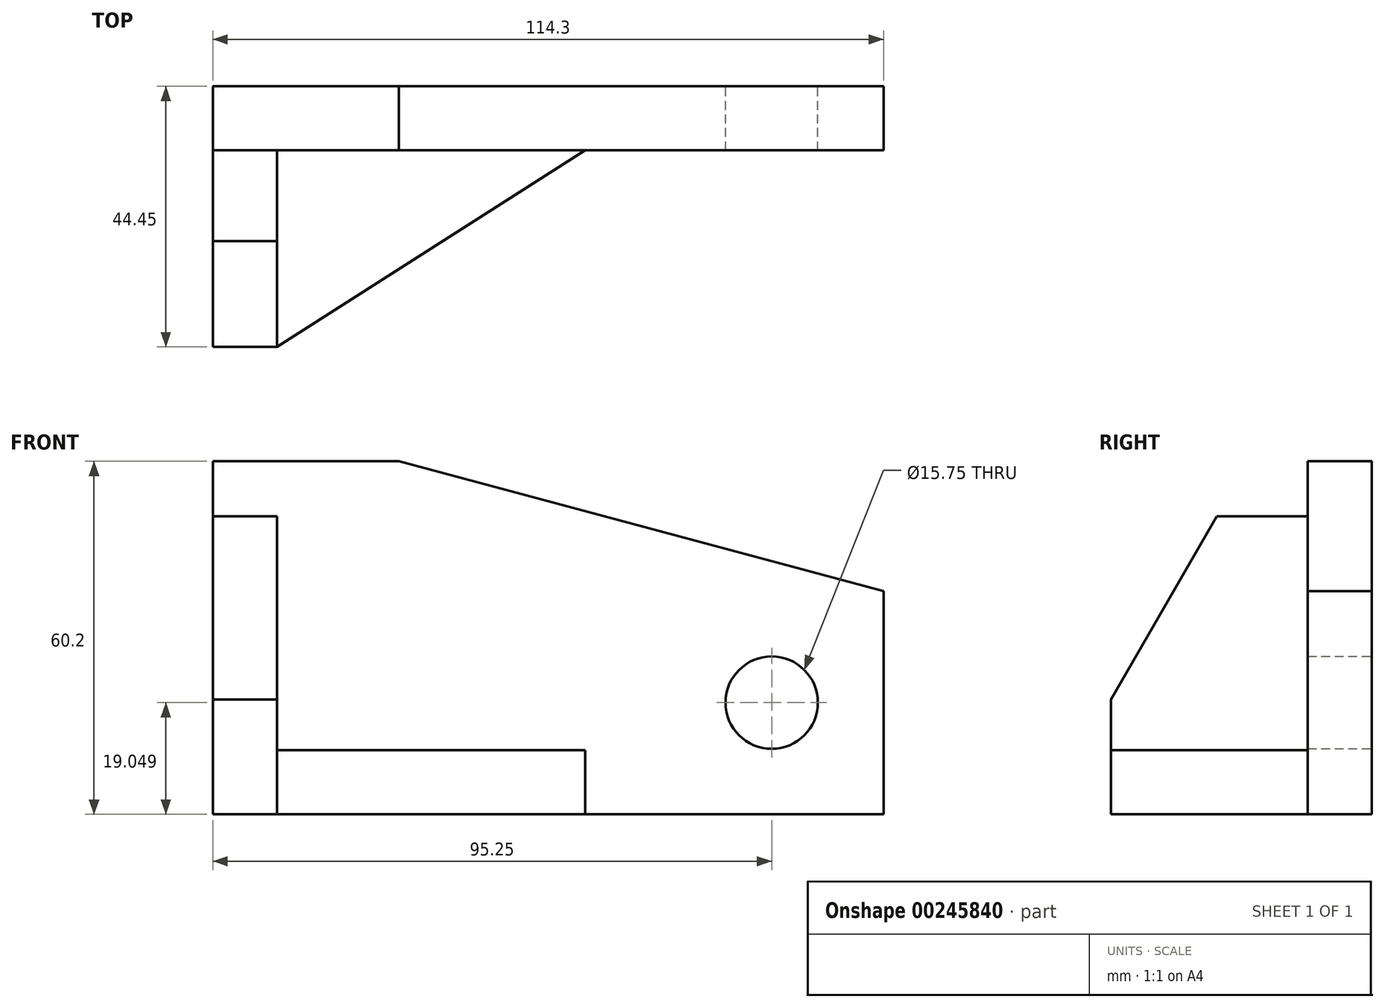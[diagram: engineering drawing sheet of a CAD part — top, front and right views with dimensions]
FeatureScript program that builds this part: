
annotation { "Feature Type Name" : "Feature", "Feature Type Description" : "" }
export const myFeature = defineFeature(function(context is Context, id is Id, definition is map)
    precondition{}
    {
        {
            var Q0;
            Q0=qCreatedBy(makeId("Front.planeOp"),FACE);
            var sketch = newSketch(context, id + "F0", { "sketchPlane" : qUnion([Q0])});
            skLineSegment(sketch, "E0", {"start": v(-31.75, 44.57) * mm, "end": v(0, 44.57) * mm});
            skLineSegment(sketch, "E1", {"start": v(-31.75, 44.57) * mm, "end": v(-31.75, -15.63) * mm});
            skLineSegment(sketch, "E2", {"start": v(0, 44.57) * mm, "end": v(82.55, 22.45) * mm});
            skLineSegment(sketch, "E3", {"start": v(82.55, 22.45) * mm, "end": v(82.55, -15.63) * mm});
            skLineSegment(sketch, "E4", {"start": v(0, 44.57) * mm, "end": v(82.55, 44.57) * mm, "construction": true});
            skCircle(sketch, "E5", {"center": v(63.5, 3.42) * mm, "radius": 7.87 * mm});
            skLineSegment(sketch, "E6", {"start": v(-31.75, -15.63) * mm, "end": v(82.55, -15.63) * mm});
            skSolve(sketch);
        }
        {
            var Q0;
            Q0=makeQuery(id+"F0.imprint","IMPRINT",FACE,{"disambiguationData":[TD([[makeQuery(id+"F0.imprint","IMPRINT",EDGE,{"derivedFrom":sQuery(id+"F0.wireOp",EDGE,"E0")}),-1.0]])]});
            extrude(context, id + "F1", {"entities" : qUnion([Q0]), "depth" : 10.92 * mm});
        }
        {
            var Q0;
            Q0=makeQuery(id+"F1.opExtrude","CAP_FACE",FACE,{"disambiguationData":[OSD([sQuery(id+"F0.wireOp",EDGE,"E0"),sQuery(id+"F0.wireOp",EDGE,"E1"),sQuery(id+"F0.wireOp",EDGE,"M5BrMvDx-n5uG-F129-FPIv-kFGHig4mUBjp"),sQuery(id+"F0.wireOp",EDGE,"E2"),sQuery(id+"F0.wireOp",EDGE,"E3"),sQuery(id+"F0.wireOp",EDGE,"g6csuxKe-7Has-kLSk-ZCsx-rTZJBOn1irfz"),sQuery(id+"F0.wireOp",EDGE,"E5")])],"isStart":false});
            var sketch = newSketch(context, id + "F2", { "sketchPlane" : qUnion([Q0])});
            skLineSegment(sketch, "E7", {"start": v(-20.83, -15.63) * mm, "end": v(-20.83, 35.17) * mm});
            skLineSegment(sketch, "E8", {"start": v(-20.83, 35.17) * mm, "end": v(-31.75, 35.17) * mm});
            skSolve(sketch);
        }
        {
            var Q0;
            {var subQ0=sQuery(id+"F2.wireOp",EDGE,"E7");Q0=makeQuery(id+"F2.imprint","IMPRINT",FACE,{"disambiguationData":[TD([[makeQuery(id+"F2.imprint","IMPRINT",EDGE,{"derivedFrom":subQ0}),1.0]])]});}
            extrude(context, id + "F3", {"entities" : qUnion([Q0]), "operationType" : NewBodyOperationType.ADD, "depth" : 33.53 * mm});
        }
        {
            var Q0;
            Q0=makeQuery(id+"F3.opExtrude","CAP_EDGE",EDGE,{"disambiguationData":[OSD([sQuery(id+"F2.wireOp",EDGE,"E8")])],"isStart":false});
            chamfer(context, id + "F4", {"entities" : qUnion([Q0]), "chamferType" : ChamferType.OFFSET_ANGLE, "width" : 31.24 * mm, "oppositeDirection" : false, "angle" : 30 * degree, "tangentPropagation" : true});
        }
        {
            var Q0;
            Q0=makeQuery(id+"F1.opExtrude","CAP_FACE",FACE,{"disambiguationData":[OSD([sQuery(id+"F0.wireOp",EDGE,"E0"),sQuery(id+"F0.wireOp",EDGE,"E1"),sQuery(id+"F0.wireOp",EDGE,"M5BrMvDx-n5uG-F129-FPIv-kFGHig4mUBjp"),sQuery(id+"F0.wireOp",EDGE,"E2"),sQuery(id+"F0.wireOp",EDGE,"E3"),sQuery(id+"F0.wireOp",EDGE,"g6csuxKe-7Has-kLSk-ZCsx-rTZJBOn1irfz"),sQuery(id+"F0.wireOp",EDGE,"E5")])],"isStart":false});
            var sketch = newSketch(context, id + "F5", { "sketchPlane" : qUnion([Q0])});
            skLineSegment(sketch, "E9", {"start": v(-20.83, -4.7) * mm, "end": v(31.75, -4.7) * mm});
            skLineSegment(sketch, "E10", {"start": v(31.75, -4.7) * mm, "end": v(31.75, -15.63) * mm});
            skSolve(sketch);
        }
        {
            var Q0;
            {var subQ0=sQuery(id+"F5.wireOp",EDGE,"E9");Q0=makeQuery(id+"F5.imprint","IMPRINT",FACE,{"disambiguationData":[TD([[makeQuery(id+"F5.imprint","IMPRINT",EDGE,{"derivedFrom":subQ0}),-1.0]])]});}
            extrude(context, id + "F6", {"entities" : qUnion([Q0]), "operationType" : NewBodyOperationType.ADD, "depth" : 33.53 * mm});
        }
        {
            var Q0;
            Q0=makeQuery(id+"F6.opExtrude","SWEPT_FACE",FACE,{"disambiguationData":[OSD([sQuery(id+"F5.wireOp",EDGE,"E9")])]});
            var sketch = newSketch(context, id + "F7", { "sketchPlane" : qUnion([Q0])});
            skLineSegment(sketch, "E11", {"start": v(-20.83, -44.45) * mm, "end": v(31.75, -10.92) * mm});
            skSolve(sketch);
        }
        {
            var Q0;
            Q0=makeQuery(id+"F7.imprint","IMPRINT",FACE,{"disambiguationData":[TD([[makeQuery(id+"F7.imprint","IMPRINT",EDGE,{"derivedFrom":sQuery(id+"F7.wireOp",EDGE,"E11")}),-1.0]])]});
            extrude(context, id + "F8", {"entities" : qUnion([Q0]), "operationType" : NewBodyOperationType.REMOVE, "oppositeDirection" : true, "depth" : 10.92 * mm});
        }
    });
